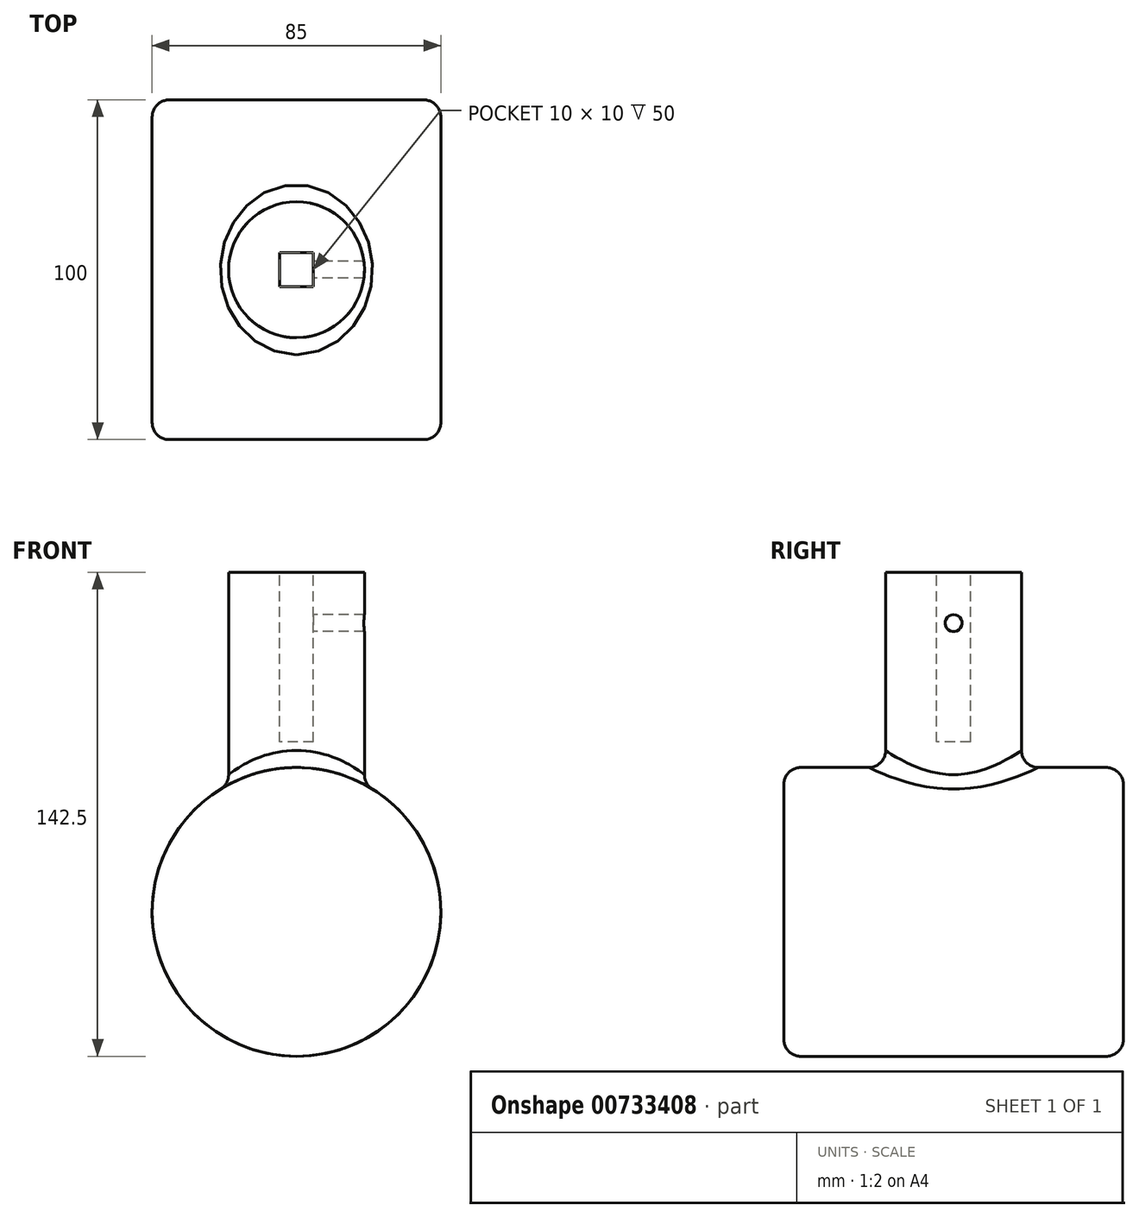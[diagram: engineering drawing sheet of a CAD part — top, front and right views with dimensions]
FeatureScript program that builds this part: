
annotation { "Feature Type Name" : "Feature", "Feature Type Description" : "" }
export const myFeature = defineFeature(function(context is Context, id is Id, definition is map)
    precondition{}
    {
        {
            var Q0;
            Q0=qCreatedBy(makeId("Front.planeOp"),FACE);
            var sketch = newSketch(context, id + "F0", { "sketchPlane" : qUnion([Q0])});
            skCircle(sketch, "E0", {"center": v(0, 0) * mm, "radius": 42.5 * mm});
            skSolve(sketch);
        }
        {
            var Q0;
            Q0=makeQuery(id+"F0.imprint","IMPRINT",FACE,{"disambiguationData":[TD([[makeQuery(id+"F0.imprint","IMPRINT",EDGE,{"derivedFrom":sQuery(id+"F0.wireOp",EDGE,"E0")}),1.0]])]});
            extrude(context, id + "F1", {"entities" : qUnion([Q0]), "endBound" : BoundingType.SYMMETRIC, "depth" : 100 * mm, "offsetDistance" : 25 * mm});
        }
        {
            var Q0;
            Q0=qCreatedBy(makeId("Top.planeOp"),FACE);
            var sketch = newSketch(context, id + "F2", { "sketchPlane" : qUnion([Q0])});
            skCircle(sketch, "E1", {"center": v(0, 0) * mm, "radius": 20 * mm});
            skSolve(sketch);
        }
        {
            var Q0;
            Q0 = qSketchRegion(id + "F2", true);
            extrude(context, id + "F3", {"entities" : qUnion([Q0]), "operationType" : NewBodyOperationType.ADD, "depth" : 100 * mm, "offsetDistance" : 25 * mm});
        }
        {
            var Q0;
            Q0=makeQuery(id+"F3.opExtrude","CAP_FACE",FACE,{"disambiguationData":[OSD([sQuery(id+"F2.wireOp",EDGE,"E1")])],"isStart":false});
            var sketch = newSketch(context, id + "F4", { "sketchPlane" : qUnion([Q0])});
            skLineSegment(sketch, "E2.bottom", {"start": v(5, 5) * mm, "end": v(-5, 5) * mm});
            skLineSegment(sketch, "E2.top", {"start": v(5, -5) * mm, "end": v(-5, -5) * mm});
            skLineSegment(sketch, "E2.left", {"start": v(5, 5) * mm, "end": v(5, -5) * mm});
            skLineSegment(sketch, "E2.right", {"start": v(-5, 5) * mm, "end": v(-5, -5) * mm});
            skPoint(sketch, "E2.middle", {"position": v(0, 0) * mm});
            skSolve(sketch);
        }
        {
            var Q0;
            Q0 = qSketchRegion(id + "F4", true);
            extrude(context, id + "F5", {"entities" : qUnion([Q0]), "operationType" : NewBodyOperationType.REMOVE, "oppositeDirection" : true, "depth" : 50 * mm, "offsetDistance" : 25 * mm});
        }
        {
            var Q0;
            Q0=qCreatedBy(makeId("Right.planeOp"),FACE);
            var sketch = newSketch(context, id + "F6", { "sketchPlane" : qUnion([Q0])});
            skCircle(sketch, "E3", {"center": v(0, 85) * mm, "radius": 2.5 * mm});
            skSolve(sketch);
        }
        {
            var Q0;
            Q0=makeQuery(id+"F6.imprint","IMPRINT",FACE,{"disambiguationData":[TD([[makeQuery(id+"F6.imprint","IMPRINT",EDGE,{"derivedFrom":sQuery(id+"F6.wireOp",EDGE,"E3")}),1.0]])]});
            var Q1;
            Q1=sQuery(id+"F6.wireOp",EDGE,"E3");
            extrude(context, id + "F7", {"entities" : qUnion([Q0]), "operationType" : NewBodyOperationType.REMOVE, "surfaceEntities" : qUnion([Q1]), "depth" : 25 * mm, "offsetDistance" : 25 * mm});
        }
        {
            var Q0;
            Q0=makeQuery(id+"F3.boolean.opBoolean","INTERSECT",EDGE,{"derivedFrom":[makeQuery(id+"F1.opExtrude","SWEPT_FACE",FACE,{"disambiguationData":[OSD([sQuery(id+"F0.wireOp",EDGE,"E0")])]}),makeQuery(id+"F3.opExtrude","SWEPT_FACE",FACE,{"disambiguationData":[OSD([sQuery(id+"F2.wireOp",EDGE,"E1")])]})]});
            fillet(context, id + "F8", {"entities" : qUnion([Q0]), "radius" : 5 * mm, "tangentPropagation" : true, "allowEdgeOverflow" : false});
        }
        {
            var Q0;
            Q0=makeQuery(id+"F1.opExtrude","CAP_EDGE",EDGE,{"disambiguationData":[OSD([sQuery(id+"F0.wireOp",EDGE,"E0")])],"isStart":false});
            fillet(context, id + "F9", {"entities" : qUnion([Q0]), "radius" : 5 * mm, "tangentPropagation" : true, "allowEdgeOverflow" : false});
        }
        {
            var Q0;
            Q0=makeQuery(id+"F1.opExtrude","CAP_EDGE",EDGE,{"disambiguationData":[OSD([sQuery(id+"F0.wireOp",EDGE,"E0")])],"isStart":true});
            fillet(context, id + "F10", {"entities" : qUnion([Q0]), "radius" : 5 * mm, "tangentPropagation" : true, "allowEdgeOverflow" : false});
        }
    });
